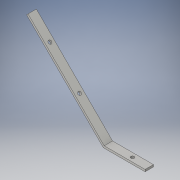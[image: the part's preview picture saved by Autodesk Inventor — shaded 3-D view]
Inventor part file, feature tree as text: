
AUTODESK INVENTOR PART (.ipt)
format: ipt  version: 2016 (Build 200138000, 138)  size: 119,808 bytes
history: native  units: in
note: dims shown in document units (in); Inventor stores cm internally (conversion verified against a paired STEP export)
features: extrude x3, sketch x3
ambient origin geometry x8: Origin, YZ Plane, XZ Plane, XY Plane, X Axis, Y Axis, Z Axis, Center Point
bodies: Solid1 (feature_tree)
feature tree (6):
  extrude  "Extrusion1"  Depth=5.1181in
  extrude  "Extrusion2"  Depth=0.0984in
  extrude  "Extrusion3"  TaperAngle=90.0deg  [1 undecoded]
  sketch  "Sketch1"  dims[d0=1.9685in d1=5.1181in]
  sketch  "Sketch2"  dims[d2=135.0deg d3=0.0984in]
  sketch  "Sketch3"  dims[d4=45.0deg d5=90.0deg d6=0.0984in d7=0.3937in d8=0.0in d9=1.1811in d10=0.1575in d11=0.3937in d12=0.0in d13=1.9685in d14=0.0in d15=1.9685in d16=0.0in d17=0.1575in d18=0.1575in d19=0.3937in d20=0.0in]
note: 1 required parameter value undecoded (feature->parameter linkage not recoverable at this tier; creation-order binding heuristic only, values carry confidence <= 0.55)
